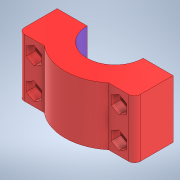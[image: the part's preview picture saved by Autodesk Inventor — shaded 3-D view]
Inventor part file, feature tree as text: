
AUTODESK INVENTOR PART (.ipt)
format: ipt  version: 2020.2 (Build 242310000, 310)  size: 246,784 bytes
history: native  units: mm
features: extrude x4, sketch x4, fillet x2, hole x1
ambient origin geometry x8: Origin, YZ Plane, XZ Plane, XY Plane, X Axis, Y Axis, Z Axis, Center Point
bodies: Solido1 (feature_tree)
feature tree (11):
  extrude  "Estrusione1"  Depth=20.0mm TaperAngle=0.0deg
  extrude  "Estrusione2"  Depth=30.0mm TaperAngle=0.0deg
  hole  "Foro3"  [1 undecoded]
  extrude  "Estrusione4"  Depth=60.0mm
  fillet  "Raccordo1"  Radius=7.0mm
  fillet  "Raccordo2"  Radius=22.0mm
  extrude  "Estrusione5"  TaperAngle=90.0deg  [1 undecoded]
  sketch  "Schizzo1"
  sketch  "Schizzo2"
  sketch  "Schizzo7"
  sketch  "Schizzo9"
note: 2 required parameter values undecoded (feature->parameter linkage not recoverable at this tier; creation-order binding heuristic only, values carry confidence <= 0.55)
